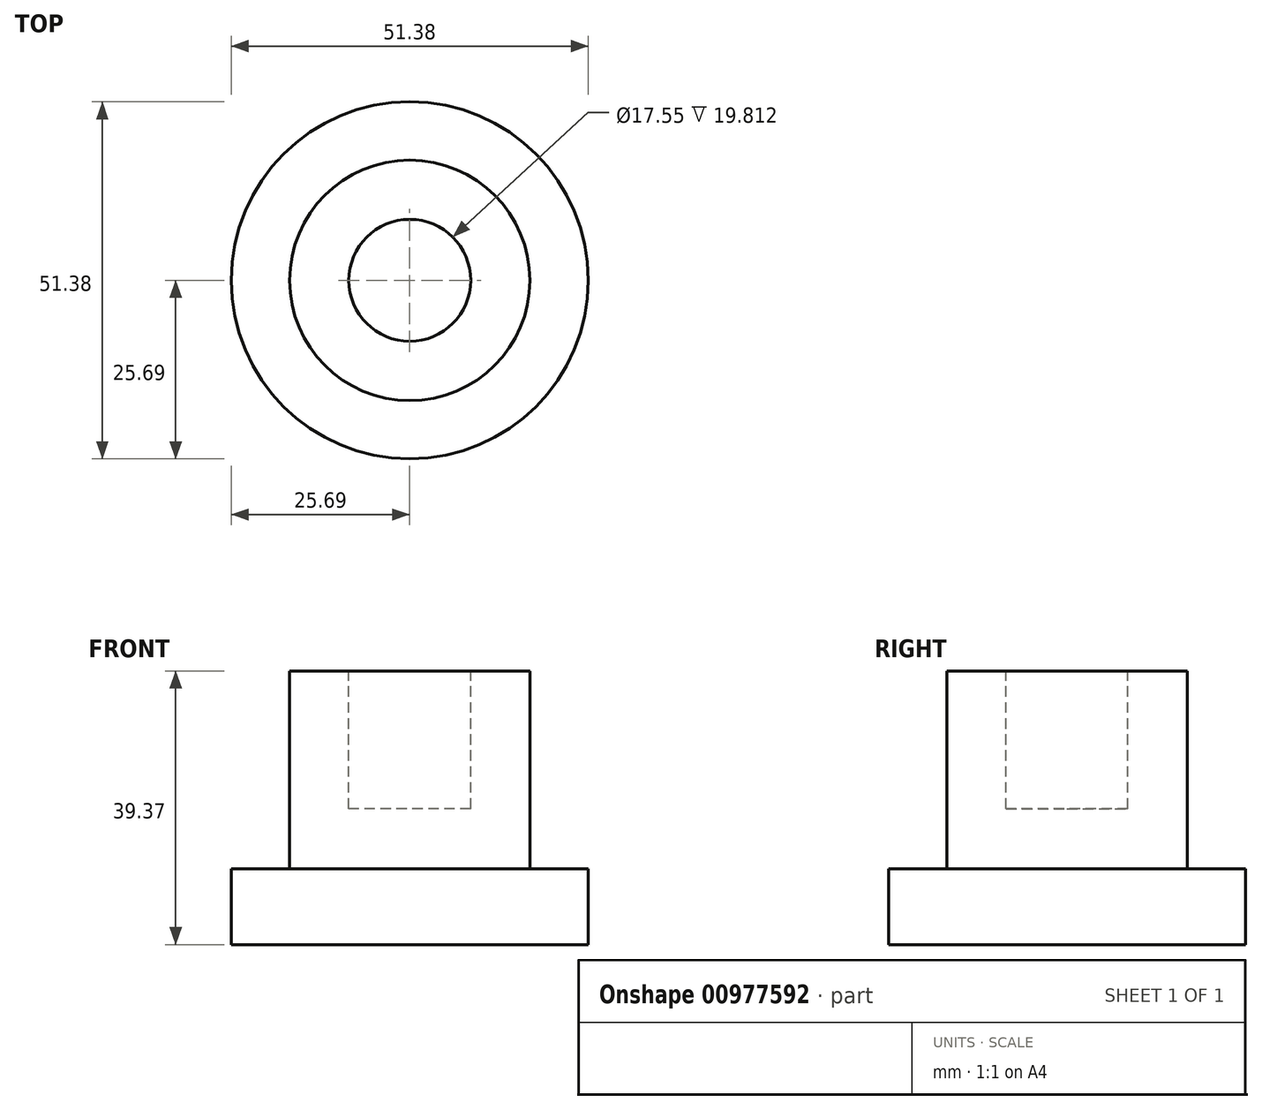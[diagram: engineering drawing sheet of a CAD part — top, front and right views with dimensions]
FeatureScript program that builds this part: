
annotation { "Feature Type Name" : "Feature", "Feature Type Description" : "" }
export const myFeature = defineFeature(function(context is Context, id is Id, definition is map)
    precondition{}
    {
        {
            var Q0;
            Q0=qCreatedBy(makeId("Top.planeOp"),FACE);
            var sketch = newSketch(context, id + "F0", { "sketchPlane" : qUnion([Q0])});
            skCircle(sketch, "E0", {"center": v(0, 0) * mm, "radius": 17.3 * mm});
            skCircle(sketch, "E1", {"center": v(0, 0) * mm, "radius": 25.69 * mm});
            skSolve(sketch);
        }
        {
            var Q0;
            Q0 = qSketchRegion(id + "F0", true);
            var Q1;
            Q1=makeQuery(id+"F0.imprint","IMPRINT",FACE,{"disambiguationData":[TD([[makeQuery(id+"F0.imprint","IMPRINT",EDGE,{"derivedFrom":sQuery(id+"F0.wireOp",EDGE,"E0")}),1.0]])]});
            extrude(context, id + "F1", {"entities" : qUnion([Q0, Q1]), "depth" : 10.92 * mm, "offsetDistance" : 25.4 * mm});
        }
        {
            var Q0;
            Q0=makeQuery(id+"F0.imprint","IMPRINT",FACE,{"disambiguationData":[TD([[makeQuery(id+"F0.imprint","IMPRINT",EDGE,{"derivedFrom":sQuery(id+"F0.wireOp",EDGE,"E0")}),1.0]])]});
            extrude(context, id + "F2", {"entities" : qUnion([Q0]), "operationType" : NewBodyOperationType.ADD, "depth" : 39.37 * mm, "offsetDistance" : 25.4 * mm});
        }
        {
            var Q0;
            Q0=makeQuery(id+"F2.opExtrude","CAP_FACE",FACE,{"disambiguationData":[OSD([sQuery(id+"F0.wireOp",EDGE,"E0")])],"isStart":false});
            var sketch = newSketch(context, id + "F3", { "sketchPlane" : qUnion([Q0])});
            skCircle(sketch, "E2", {"center": v(0, 0) * mm, "radius": 8.77 * mm});
            skSolve(sketch);
        }
        {
            var Q0;
            Q0=makeQuery(id+"F3.imprint","IMPRINT",FACE,{"disambiguationData":[TD([[makeQuery(id+"F3.imprint","IMPRINT",EDGE,{"derivedFrom":sQuery(id+"F3.wireOp",EDGE,"E2")}),1.0]])]});
            extrude(context, id + "F4", {"entities" : qUnion([Q0]), "operationType" : NewBodyOperationType.REMOVE, "oppositeDirection" : true, "depth" : 19.8 * mm, "offsetDistance" : 25.4 * mm});
        }
    });
